# Revit family: Haworth_Masters_Corner_Shell
name_source: partatom
category: Furniture Systems
revit_build: Autodesk Revit 2018 (Build: 20170223_1515(x64)
units: mm (PartAtom-declared; Revit-internal decimal feet)

## family parameters
Always vertical = Yes
Cut with Voids When Loaded = No
OmniClass Number = 23.40.70.14.64.21
OmniClass Title = Systems Furniture
Part Type = Normal
Room Calculation Point = No
Round Connector Dimension = Use Diameter
Shared = No
Work Plane-Based = No

## types (2) — shared parameters
Actual Depth Left = 24"
Actual Depth Right = 24"
Actual Height = 29 1/8"
Assembly Code = E2020200
Custom Size = No
Depth Left = 24"
Depth Right = 24"
Manufacturer = Haworth
Max. Depth = 42"
Max. Width = 42"
Min. Depth = 36"
Min. Width = 36"
Model = Haworth Masters
Revision Number = 1
Size = Verify Final Dim. w/ Haworth
Standard Depths = 36, 42 in.
Standard Widths = 36, 42 in.
Sustainability Info = https://www.haworth.com
Thickness = 1 3/16"
URL = www.haworth.com
URL - Product = https://www.haworth.com
Warranty = http://www.haworth.com

## per-type parameters (varying)
| type | Actual Depth | Actual Width | Depth | Description | Max. Depth Side | Min. Depth Side | Width |
| 42w 42d | 42" | 42" | 42" | Haworth - Masters - Corner Shell - 42w 42d | 30" | 24" | 42" |
| 36w 36d | 36" | 36" | 36" | Haworth - Masters - Corner Shell - 36w 36d | 24" | 19" | 36" |

## geometry (parser evidence)
native form markers: Sweep x4
no freeform markers — native parametric forms only
